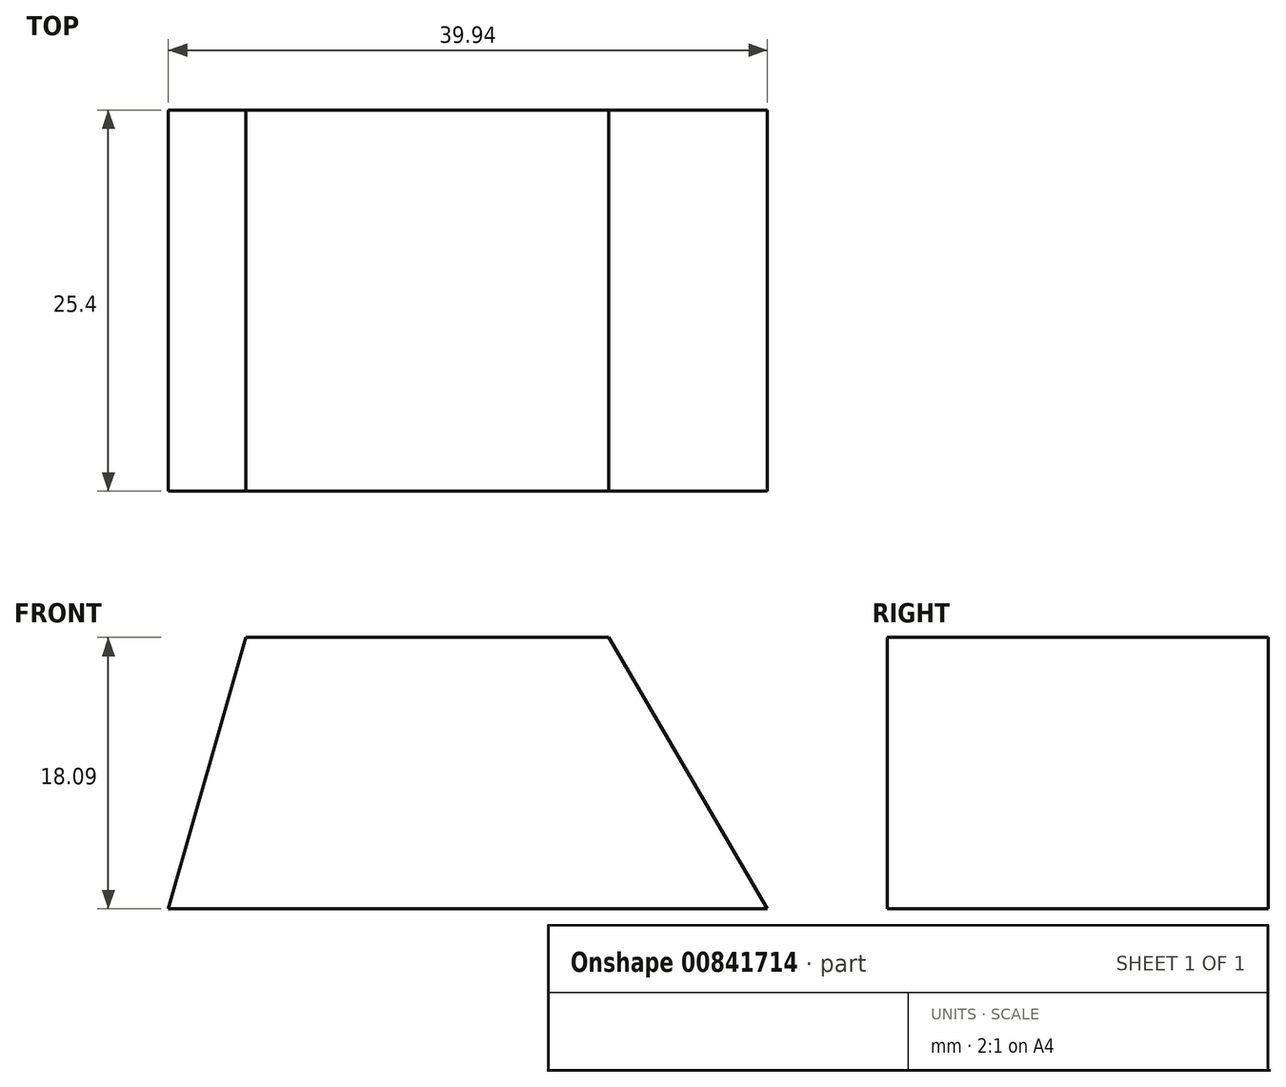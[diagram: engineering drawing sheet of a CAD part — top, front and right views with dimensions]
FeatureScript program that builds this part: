
annotation { "Feature Type Name" : "Feature", "Feature Type Description" : "" }
export const myFeature = defineFeature(function(context is Context, id is Id, definition is map)
    precondition{}
    {
        {
            var Q0;
            Q0=qCreatedBy(makeId("Front.planeOp"),FACE);
            var sketch = newSketch(context, id + "F0", { "sketchPlane" : qUnion([Q0])});
            skLineSegment(sketch, "E0", {"start": v(-50.76, 41.12) * mm, "end": v(-26.55, 41.12) * mm});
            skLineSegment(sketch, "E1", {"start": v(-26.55, 41.12) * mm, "end": v(-15.98, 23.03) * mm});
            skLineSegment(sketch, "E2", {"start": v(-55.92, 23.03) * mm, "end": v(-50.76, 41.12) * mm});
            skLineSegment(sketch, "E3", {"start": v(-55.92, 23.03) * mm, "end": v(-15.98, 23.03) * mm});
            skSolve(sketch);
        }
        {
            var Q0;
            Q0 = qSketchRegion(id + "F0", true);
            extrude(context, id + "F1", {"entities" : qUnion([Q0]), "depth" : 25.4 * mm, "offsetDistance" : 25.4 * mm});
        }
    });
